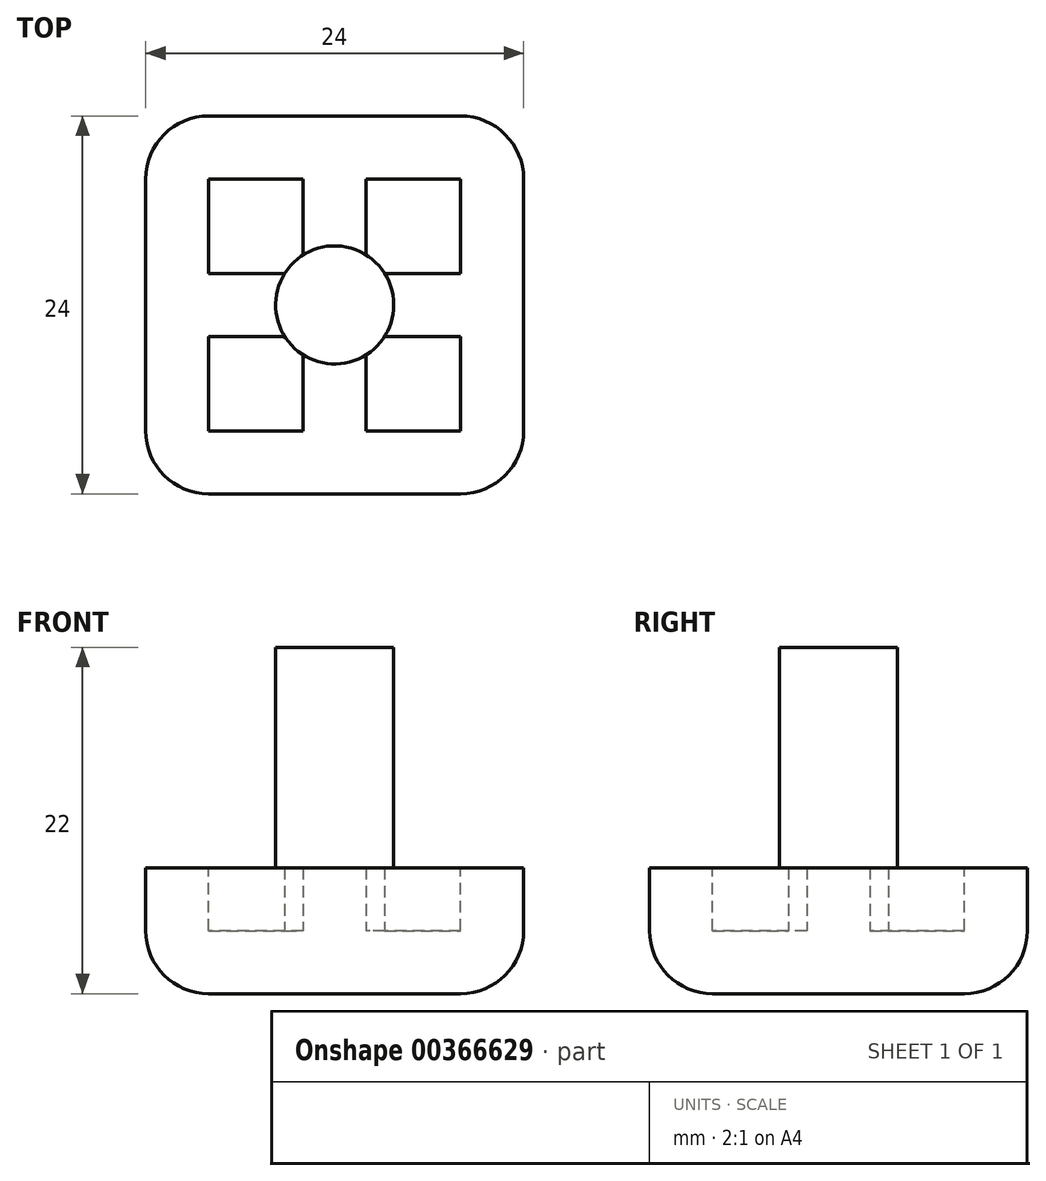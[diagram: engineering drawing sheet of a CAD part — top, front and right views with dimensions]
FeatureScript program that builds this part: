
annotation { "Feature Type Name" : "Feature", "Feature Type Description" : "" }
export const myFeature = defineFeature(function(context is Context, id is Id, definition is map)
    precondition{}
    {
        {
            var Q0;
            Q0=qCreatedBy(makeId("Top.planeOp"),FACE);
            var sketch = newSketch(context, id + "F0", { "sketchPlane" : qUnion([Q0])});
            skLineSegment(sketch, "E0.bottom", {"start": v(12, -12) * mm, "end": v(-12, -12) * mm});
            skLineSegment(sketch, "E0.top", {"start": v(12, 12) * mm, "end": v(-12, 12) * mm});
            skLineSegment(sketch, "E0.left", {"start": v(12, -12) * mm, "end": v(12, 12) * mm});
            skLineSegment(sketch, "E0.right", {"start": v(-12, -12) * mm, "end": v(-12, 12) * mm});
            skPoint(sketch, "E0.middle", {"position": v(0, 0) * mm});
            skSolve(sketch);
        }
        {
            var Q0;
            Q0 = qSketchRegion(id + "F0", true);
            extrude(context, id + "F1", {"entities" : qUnion([Q0]), "depth" : 8 * mm, "offsetDistance" : 25 * mm});
        }
        {
            var Q0;
            Q0=makeQuery(id+"F1.opExtrude","CAP_FACE",FACE,{"disambiguationData":[OSD([sQuery(id+"F0.wireOp",EDGE,"E0.bottom"),sQuery(id+"F0.wireOp",EDGE,"E0.top"),sQuery(id+"F0.wireOp",EDGE,"E0.left"),sQuery(id+"F0.wireOp",EDGE,"E0.right")])],"isStart":true});
            var Q1;
            Q1=makeQuery(id+"F1.opExtrude","SWEPT_EDGE",EDGE,{"disambiguationData":[OSD([sQuery(id+"F0.wireOp",EDGE,"E0.bottom"),sQuery(id+"F0.wireOp",EDGE,"E0.left")])]});
            var Q2;
            Q2=makeQuery(id+"F1.opExtrude","SWEPT_EDGE",EDGE,{"disambiguationData":[OSD([sQuery(id+"F0.wireOp",EDGE,"E0.bottom"),sQuery(id+"F0.wireOp",EDGE,"E0.right")])]});
            var Q3;
            Q3=makeQuery(id+"F1.opExtrude","SWEPT_EDGE",EDGE,{"disambiguationData":[OSD([sQuery(id+"F0.wireOp",EDGE,"E0.top"),sQuery(id+"F0.wireOp",EDGE,"E0.right")])]});
            var Q4;
            Q4=makeQuery(id+"F1.opExtrude","SWEPT_EDGE",EDGE,{"disambiguationData":[OSD([sQuery(id+"F0.wireOp",EDGE,"E0.top"),sQuery(id+"F0.wireOp",EDGE,"E0.left")])]});
            fillet(context, id + "F2", {"entities" : qUnion([Q0, Q1, Q2, Q3, Q4]), "radius" : 4 * mm, "tangentPropagation" : true, "allowEdgeOverflow" : false});
        }
        {
            var Q0;
            Q0=makeQuery(id+"F1.opExtrude","CAP_FACE",FACE,{"disambiguationData":[OSD([sQuery(id+"F0.wireOp",EDGE,"E0.bottom"),sQuery(id+"F0.wireOp",EDGE,"E0.top"),sQuery(id+"F0.wireOp",EDGE,"E0.left"),sQuery(id+"F0.wireOp",EDGE,"E0.right")])],"isStart":false});
            var sketch = newSketch(context, id + "F3", { "sketchPlane" : qUnion([Q0])});
            skLineSegment(sketch, "E1.bottom", {"start": v(8, 8) * mm, "end": v(-8, 8) * mm});
            skLineSegment(sketch, "E1.top", {"start": v(8, -8) * mm, "end": v(-8, -8) * mm});
            skLineSegment(sketch, "E1.left", {"start": v(8, 8) * mm, "end": v(8, -8) * mm});
            skLineSegment(sketch, "E1.right", {"start": v(-8, 8) * mm, "end": v(-8, -8) * mm});
            skPoint(sketch, "E1.middle", {"position": v(0, 0) * mm});
            skLineSegment(sketch, "E2", {"start": v(-8, -2) * mm, "end": v(8, -2) * mm});
            skLineSegment(sketch, "E3", {"start": v(-8, 2) * mm, "end": v(8, 2) * mm});
            skLineSegment(sketch, "E4", {"start": v(-2, -8) * mm, "end": v(-2, 8) * mm});
            skLineSegment(sketch, "E5", {"start": v(2, -8) * mm, "end": v(2, 8) * mm});
            skSolve(sketch);
        }
        {
            var Q0;
            {var subQ0=sQuery(id+"F3.wireOp",EDGE,"E1.left");var subQ1=sQuery(id+"F3.wireOp",EDGE,"E1.bottom");var subQ2=makeQuery(id+"F3.imprint","INTERSECT",VERTEX,{"derivedFrom":[subQ1,subQ0]});Q0=makeQuery(id+"F3.imprint","IMPRINT",FACE,{"disambiguationData":[TD([[makeQuery(id+"F3.imprint","IMPRINT",EDGE,{"disambiguationData":[TD([[subQ2,-1.0]])],"derivedFrom":subQ1}),1.0]])]});}
            var Q1;
            {var subQ0=sQuery(id+"F3.wireOp",EDGE,"E1.right");var subQ1=sQuery(id+"F3.wireOp",EDGE,"E1.bottom");var subQ2=makeQuery(id+"F3.imprint","INTERSECT",VERTEX,{"derivedFrom":[subQ1,subQ0]});Q1=makeQuery(id+"F3.imprint","IMPRINT",FACE,{"disambiguationData":[TD([[makeQuery(id+"F3.imprint","IMPRINT",EDGE,{"disambiguationData":[TD([[subQ2,1.0]])],"derivedFrom":subQ1}),1.0]])]});}
            var Q2;
            {var subQ0=sQuery(id+"F3.wireOp",EDGE,"E1.left");var subQ1=sQuery(id+"F3.wireOp",EDGE,"E1.top");var subQ2=makeQuery(id+"F3.imprint","INTERSECT",VERTEX,{"derivedFrom":[subQ1,subQ0]});Q2=makeQuery(id+"F3.imprint","IMPRINT",FACE,{"disambiguationData":[TD([[makeQuery(id+"F3.imprint","IMPRINT",EDGE,{"disambiguationData":[TD([[subQ2,-1.0]])],"derivedFrom":subQ1}),-1.0]])]});}
            var Q3;
            {var subQ0=sQuery(id+"F3.wireOp",EDGE,"E1.right");var subQ1=sQuery(id+"F3.wireOp",EDGE,"E1.top");var subQ2=makeQuery(id+"F3.imprint","INTERSECT",VERTEX,{"derivedFrom":[subQ1,subQ0]});Q3=makeQuery(id+"F3.imprint","IMPRINT",FACE,{"disambiguationData":[TD([[makeQuery(id+"F3.imprint","IMPRINT",EDGE,{"disambiguationData":[TD([[subQ2,1.0]])],"derivedFrom":subQ1}),-1.0]])]});}
            extrude(context, id + "F4", {"entities" : qUnion([Q0, Q1, Q2, Q3]), "operationType" : NewBodyOperationType.REMOVE, "oppositeDirection" : true, "depth" : 4 * mm, "offsetDistance" : 25 * mm});
        }
        {
            var Q0;
            Q0=makeQuery(id+"F4.boolean.opBoolean","COPY",FACE,{"derivedFrom":makeQuery(id+"F4.opExtrude","CAP_FACE",FACE,{"disambiguationData":[OSD([sQuery(id+"F3.wireOp",EDGE,"E1.top"),sQuery(id+"F3.wireOp",EDGE,"E1.left"),sQuery(id+"F3.wireOp",EDGE,"E2"),sQuery(id+"F3.wireOp",EDGE,"E5")])],"isStart":false})});
            var sketch = newSketch(context, id + "F5", { "sketchPlane" : qUnion([Q0])});
            skCircle(sketch, "E6", {"center": v(0, 0) * mm, "radius": 3.75 * mm});
            skSolve(sketch);
        }
        {
            var Q0;
            Q0 = qSketchRegion(id + "F5", true);
            extrude(context, id + "F6", {"entities" : qUnion([Q0]), "operationType" : NewBodyOperationType.ADD, "depth" : 18 * mm, "offsetDistance" : 25 * mm});
        }
    });
